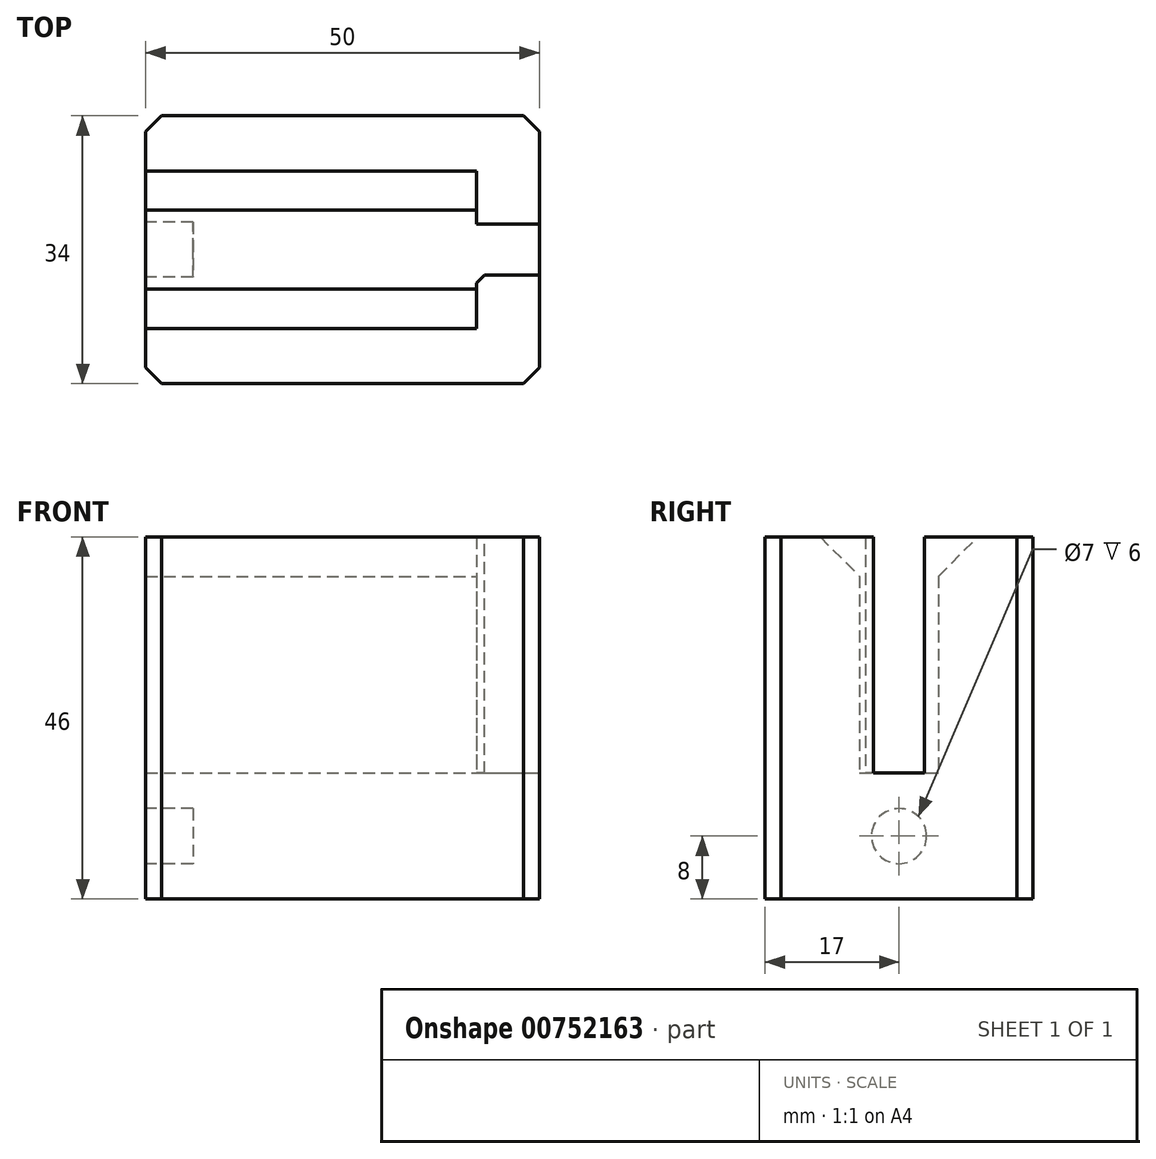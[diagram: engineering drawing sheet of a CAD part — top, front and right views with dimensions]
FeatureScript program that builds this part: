
annotation { "Feature Type Name" : "Feature", "Feature Type Description" : "" }
export const myFeature = defineFeature(function(context is Context, id is Id, definition is map)
    precondition{}
    {
        {
            var Q0;
            Q0=qCreatedBy(makeId("Front.planeOp"),FACE);
            var sketch = newSketch(context, id + "F0", { "sketchPlane" : qUnion([Q0])});
            skLineSegment(sketch, "E0.bottom", {"start": v(-25, 8) * mm, "end": v(-20, 8) * mm});
            skLineSegment(sketch, "E0.top", {"start": v(-25, -8) * mm, "end": v(25, -8) * mm});
            skLineSegment(sketch, "E0.left", {"start": v(-25, 8) * mm, "end": v(-25, -8) * mm});
            skLineSegment(sketch, "E0.right", {"start": v(25, 38) * mm, "end": v(25, -8) * mm});
            skPoint(sketch, "E0.middle", {"position": v(0, 0) * mm});
            skLineSegment(sketch, "E1.0", {"start": v(-20, 8) * mm, "end": v(-20, 8) * mm});
            skLineSegment(sketch, "E2.0", {"start": v(-20, 8) * mm, "end": v(17, 8) * mm});
            skLineSegment(sketch, "E3.0", {"start": v(17, 38) * mm, "end": v(17, 8) * mm});
            skPoint(sketch, "E4.orphan", {"position": v(25, 8) * mm});
            skLineSegment(sketch, "E5.trimOffspring", {"start": v(17, 38) * mm, "end": v(25, 38) * mm});
            skSolve(sketch);
        }
        {
            var Q0;
            Q0=qSketchRegion(id+"F0",true);
            extrude(context, id + "F1", {"entities" : qUnion([Q0]), "depth" : 34 * mm, "offsetDistance" : 25 * mm});
        }
        {
            var Q0;
            Q0=makeQuery(id+"F1.opExtrude","SWEPT_FACE",FACE,{"disambiguationData":[OSD([sQuery(id+"F0.wireOp",EDGE,"E0.right")])]});
            var sketch = newSketch(context, id + "F2", { "sketchPlane" : qUnion([Q0])});
            skLineSegment(sketch, "E6.bottom", {"start": v(-20.25, 38) * mm, "end": v(-13.75, 38) * mm});
            skLineSegment(sketch, "E6.top", {"start": v(-20.25, 8) * mm, "end": v(-13.75, 8) * mm});
            skLineSegment(sketch, "E6.left", {"start": v(-20.25, 38) * mm, "end": v(-20.25, 8) * mm});
            skLineSegment(sketch, "E6.right", {"start": v(-13.75, 38) * mm, "end": v(-13.75, 8) * mm});
            skSolve(sketch);
        }
        {
            var Q0;
            Q0=qSketchRegion(id+"F2",true);
            var Q1;
            Q1=makeQuery(id+"F1.opExtrude","SWEPT_FACE",FACE,{"disambiguationData":[OSD([sQuery(id+"F0.wireOp",EDGE,"E3.0")])]});
            extrude(context, id + "F3", {"entities" : qUnion([Q0]), "operationType" : NewBodyOperationType.REMOVE, "endBound" : BoundingType.UP_TO_SURFACE, "oppositeDirection" : true, "depth" : 25 * mm, "endBoundEntityFace" : qUnion([Q1]), "offsetDistance" : 25 * mm});
        }
        {
            var Q0;
            Q0=makeQuery(id+"F1.opExtrude","SWEPT_FACE",FACE,{"disambiguationData":[OSD([sQuery(id+"F0.wireOp",EDGE,"E0.left")])]});
            var sketch = newSketch(context, id + "F4", { "sketchPlane" : qUnion([Q0])});
            skCircle(sketch, "E7", {"center": v(17, 0) * mm, "radius": 3.5 * mm});
            skSolve(sketch);
        }
        {
            var Q0;
            Q0=qSketchRegion(id+"F4",true);
            extrude(context, id + "F5", {"entities" : qUnion([Q0]), "operationType" : NewBodyOperationType.REMOVE, "oppositeDirection" : true, "depth" : 6 * mm, "offsetDistance" : 25 * mm});
        }
        {
            var Q0;
            Q0=makeQuery(id+"F3.boolean.opBoolean","MERGE",FACE,{"derivedFrom":[makeQuery(id+"F1.opExtrude","SWEPT_FACE",FACE,{"disambiguationData":[OSD([sQuery(id+"F0.wireOp",EDGE,"E0.bottom"),sQuery(id+"F0.wireOp",EDGE,"E2.0")])]})],"fromTools":[makeQuery(id+"F3.opExtrude","SWEPT_FACE",FACE,{"disambiguationData":[OSD([sQuery(id+"F2.wireOp",EDGE,"E6.top")])]})]});
            var sketch = newSketch(context, id + "F6", { "sketchPlane" : qUnion([Q0])});
            skLineSegment(sketch, "E8.bottom", {"start": v(-25, -34) * mm, "end": v(17, -34) * mm});
            skLineSegment(sketch, "E8.top", {"start": v(-25, -22) * mm, "end": v(17, -22) * mm});
            skLineSegment(sketch, "E8.left", {"start": v(-25, -34) * mm, "end": v(-25, -22) * mm});
            skLineSegment(sketch, "E8.right", {"start": v(17, -34) * mm, "end": v(17, -22) * mm});
            skLineSegment(sketch, "E9.bottom", {"start": v(-25, 0) * mm, "end": v(17, 0) * mm});
            skLineSegment(sketch, "E9.top", {"start": v(-25, -12) * mm, "end": v(17, -12) * mm});
            skLineSegment(sketch, "E9.left", {"start": v(-25, 0) * mm, "end": v(-25, -12) * mm});
            skLineSegment(sketch, "E9.right", {"start": v(17, 0) * mm, "end": v(17, -12) * mm});
            skSolve(sketch);
        }
        {
            var Q0;
            Q0=qSketchRegion(id+"F6",true);
            var Q1;
            {var subQ0=sQuery(id+"F0.wireOp",EDGE,"E5.trimOffspring");Q1=makeQuery(id+"F3.boolean.opBoolean","SPLIT",FACE,{"disambiguationData":[TD([makeQuery(id+"F3.opExtrude","SWEPT_FACE",FACE,{"disambiguationData":[OSD([sQuery(id+"F2.wireOp",EDGE,"E6.left")])]})])],"derivedFrom":makeQuery(id+"F1.opExtrude","SWEPT_FACE",FACE,{"disambiguationData":[OSD([subQ0])]})});}
            extrude(context, id + "F7", {"entities" : qUnion([Q0]), "operationType" : NewBodyOperationType.ADD, "endBound" : BoundingType.UP_TO_SURFACE, "depth" : 25 * mm, "endBoundEntityFace" : qUnion([Q1]), "offsetDistance" : 25 * mm});
        }
        {
            var Q0;
            Q0=makeQuery(id+"F7.opExtrude","CAP_EDGE",EDGE,{"disambiguationData":[OSD([sQuery(id+"F6.wireOp",EDGE,"E8.top")])],"isStart":false});
            var Q1;
            Q1=makeQuery(id+"F7.opExtrude","CAP_EDGE",EDGE,{"disambiguationData":[OSD([sQuery(id+"F6.wireOp",EDGE,"E9.top")])],"isStart":false});
            chamfer(context, id + "F8", {"entities" : qUnion([Q0, Q1]), "width" : 5 * mm, "tangentPropagation" : true});
        }
        {
            var Q0;
            Q0=makeQuery(id+"F1.opExtrude","CAP_EDGE",EDGE,{"disambiguationData":[OSD([sQuery(id+"F0.wireOp",EDGE,"E0.right")])],"isStart":false});
            var Q1;
            Q1=makeQuery(id+"F1.opExtrude","CAP_EDGE",EDGE,{"disambiguationData":[OSD([sQuery(id+"F0.wireOp",EDGE,"E0.right")])],"isStart":true});
            var Q2;
            Q2=makeQuery(id+"F7.boolean.opBoolean","MERGE",EDGE,{"derivedFrom":[makeQuery(id+"F1.opExtrude","CAP_EDGE",EDGE,{"disambiguationData":[OSD([sQuery(id+"F0.wireOp",EDGE,"E0.left")])],"isStart":false}),makeQuery(id+"F7.opExtrude","SWEPT_EDGE",EDGE,{"disambiguationData":[OSD([sQuery(id+"F6.wireOp",EDGE,"E8.bottom"),sQuery(id+"F6.wireOp",EDGE,"E8.left")])]})]});
            var Q3;
            Q3=makeQuery(id+"F7.boolean.opBoolean","MERGE",EDGE,{"derivedFrom":[makeQuery(id+"F1.opExtrude","CAP_EDGE",EDGE,{"disambiguationData":[OSD([sQuery(id+"F0.wireOp",EDGE,"E0.left")])],"isStart":true}),makeQuery(id+"F7.opExtrude","SWEPT_EDGE",EDGE,{"disambiguationData":[OSD([sQuery(id+"F6.wireOp",EDGE,"E9.bottom"),sQuery(id+"F6.wireOp",EDGE,"E9.left")])]})]});
            chamfer(context, id + "F9", {"entities" : qUnion([Q0, Q1, Q2, Q3]), "width" : 2 * mm, "tangentPropagation" : true});
        }
        {
            var Q0;
            Q0=makeQuery(id+"F3.boolean.opBoolean","COPY",EDGE,{"derivedFrom":makeQuery(id+"F3.opExtrude","CAP_EDGE",EDGE,{"disambiguationData":[OSD([sQuery(id+"F2.wireOp",EDGE,"E6.right")])],"isStart":false})});
            var Q1;
            Q1=makeQuery(id+"F3.boolean.opBoolean","COPY",EDGE,{"derivedFrom":makeQuery(id+"F3.opExtrude","CAP_EDGE",EDGE,{"disambiguationData":[OSD([sQuery(id+"F2.wireOp",EDGE,"E6.left")])],"isStart":false})});
            var Q2;
            Q2=makeQuery(id+"F3.boolean.opBoolean","COPY",EDGE,{"derivedFrom":makeQuery(id+"F3.opExtrude","CAP_EDGE",EDGE,{"disambiguationData":[OSD([sQuery(id+"F2.wireOp",EDGE,"E6.right")])],"isStart":true})});
            var Q3;
            Q3=makeQuery(id+"F3.boolean.opBoolean","COPY",EDGE,{"derivedFrom":makeQuery(id+"F3.opExtrude","CAP_EDGE",EDGE,{"disambiguationData":[OSD([sQuery(id+"F2.wireOp",EDGE,"E6.left")])],"isStart":true})});
            chamfer(context, id + "F10", {"entities" : qUnion([Q0, Q1, Q2, Q3]), "width" : 1 * mm, "tangentPropagation" : true});
        }
    });
